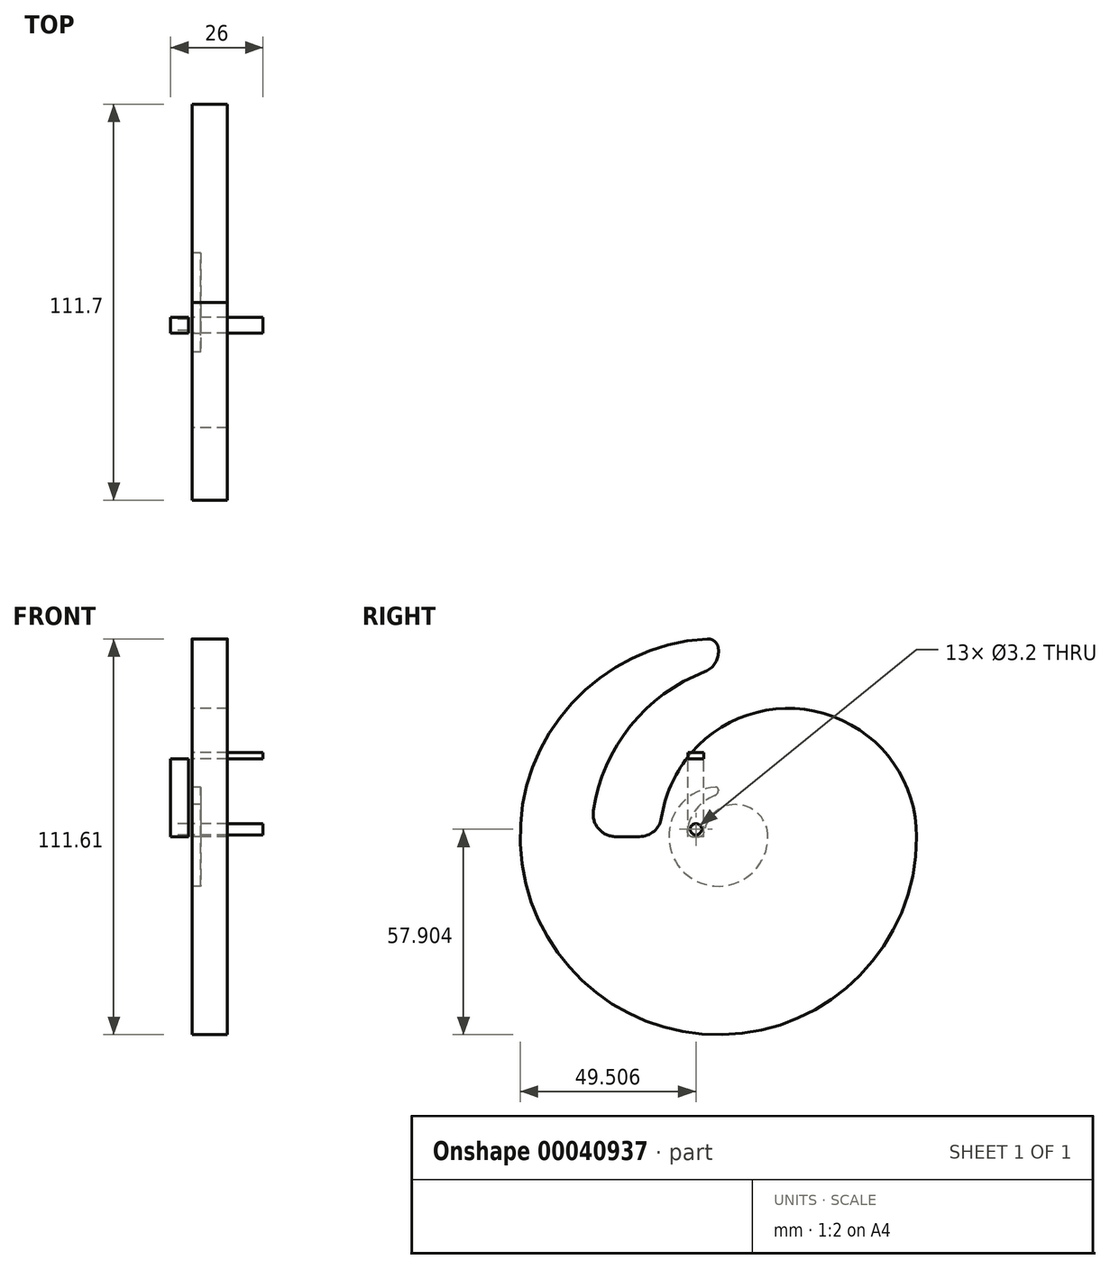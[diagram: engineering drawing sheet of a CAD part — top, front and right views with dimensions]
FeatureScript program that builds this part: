
annotation { "Feature Type Name" : "Feature", "Feature Type Description" : "" }
export const myFeature = defineFeature(function(context is Context, id is Id, definition is map)
    precondition{}
    {
        {
            var Q0;
            Q0=qCreatedBy(makeId("Right.planeOp"),FACE);
            var sketch = newSketch(context, id + "F0", { "sketchPlane" : qUnion([Q0])});
            skArc(sketch, "E0", {"start": v(-3.17, 55.76) * mm, "mid": v(-38.35, -40.6) * mm, "end": v(55.85, 0) * mm});
            skPoint(sketch, "E1", {"position": v(29.62, 47.35) * mm});
            skArc(sketch, "E2", {"start": v(55.85, 0) * mm, "mid": v(22.42, 36.03) * mm, "end": v(-16.02, 5.4) * mm});
            skArc(sketch, "E3", {"start": v(-3.76, 46.53) * mm, "mid": v(-24.8, 31.16) * mm, "end": v(-35.22, 7.28) * mm});
            skLineSegment(sketch, "E4", {"start": v(-28.94, 0) * mm, "end": v(-22.3, 0) * mm});
            skPoint(sketch, "E5.visualSharp", {"position": v(-35.75, 0) * mm});
            skArc(sketch, "E5.filletArc", {"start": v(-35.22, 7.28) * mm, "mid": v(-33.74, 2.2) * mm, "end": v(-28.94, 0) * mm});
            skPoint(sketch, "E6.visualSharp", {"position": v(-16.42, 0) * mm});
            skArc(sketch, "E6.filletArc", {"start": v(-22.3, 0) * mm, "mid": v(-18.15, 1.54) * mm, "end": v(-16.02, 5.4) * mm});
            skLineSegment(sketch, "E7", {"start": v(0, 52.76) * mm, "end": v(0, 52) * mm});
            skPoint(sketch, "E8.visualSharp", {"position": v(0, 47.8) * mm});
            skArc(sketch, "E8.filletArc", {"start": v(-3.76, 46.53) * mm, "mid": v(-1.03, 48.68) * mm, "end": v(0, 52) * mm});
            skPoint(sketch, "E9.visualSharp", {"position": v(0, 55.85) * mm});
            skArc(sketch, "E9.filletArc", {"start": v(0, 52.76) * mm, "mid": v(-0.94, 54.94) * mm, "end": v(-3.17, 55.76) * mm});
            skSolve(sketch);
        }
        {
            var Q0;
            Q0=makeQuery(id+"F0.imprint","IMPRINT",FACE,{"disambiguationData":[TD([[makeQuery(id+"F0.imprint","IMPRINT",EDGE,{"derivedFrom":sQuery(id+"F0.wireOp",EDGE,"E0")}),1.0]])]});
            extrude(context, id + "F1", {"entities" : qUnion([Q0]), "depth" : 10 * mm});
        }
        {
            var Q0;
            Q0=makeQuery(id+"F1.opExtrude","SWEPT_BODY",BODY,{"disambiguationData":[OSD([sQuery(id+"F0.wireOp",EDGE,"E0"),sQuery(id+"F0.wireOp",EDGE,"E2"),sQuery(id+"F0.wireOp",EDGE,"E3"),sQuery(id+"F0.wireOp",EDGE,"E4"),sQuery(id+"F0.wireOp",EDGE,"E5.filletArc"),sQuery(id+"F0.wireOp",EDGE,"E6.filletArc"),sQuery(id+"F0.wireOp",EDGE,"E7"),sQuery(id+"F0.wireOp",EDGE,"E8.filletArc"),sQuery(id+"F0.wireOp",EDGE,"E9.filletArc")])]});
            var Q1;
            Q1=qCreatedBy(makeId("Origin.pointOp"),VERTEX);
            transform(context, id + "F2", {"entities" : qUnion([Q0]), "transformType" : TransformType.SCALE_UNIFORMLY, "scale" : .25, "makeCopy" : true, "scalePoint" : qUnion([Q1])});
        }
        {
            var Q0;
            Q0=qCreatedBy(makeId("Right.planeOp"),FACE);
            var sketch = newSketch(context, id + "F3", { "sketchPlane" : qUnion([Q0])});
            skCircle(sketch, "E10", {"center": v(-6.34, 2.05) * mm, "radius": 1.6 * mm});
            skLineSegment(sketch, "E11.bottom", {"start": v(-4.17, 0) * mm, "end": v(-8.63, 0) * mm});
            skLineSegment(sketch, "E11.top", {"start": v(-4.17, 23.7) * mm, "end": v(-8.63, 23.7) * mm});
            skLineSegment(sketch, "E11.left", {"start": v(-4.17, 0) * mm, "end": v(-4.17, 21.95) * mm});
            skLineSegment(sketch, "E11.right", {"start": v(-8.63, 0) * mm, "end": v(-8.63, 21.95) * mm});
            skLineSegment(sketch, "E12", {"start": v(-8.63, 21.95) * mm, "end": v(-4.17, 21.95) * mm});
            skLineSegment(sketch, "E13", {"start": v(-8.63, 21.95) * mm, "end": v(-8.63, 23.7) * mm});
            skLineSegment(sketch, "E14", {"start": v(-4.17, 21.95) * mm, "end": v(-4.17, 23.7) * mm});
            skSolve(sketch);
        }
        {
            var Q0;
            Q0=makeQuery(id+"F3.imprint","IMPRINT",FACE,{"disambiguationData":[TD([[makeQuery(id+"F3.imprint","IMPRINT",EDGE,{"derivedFrom":sQuery(id+"F3.wireOp",EDGE,"E10")}),1.0]])]});
            var Q1;
            Q1=makeQuery(id+"F3.imprint","IMPRINT",FACE,{"disambiguationData":[TD([[makeQuery(id+"F3.imprint","IMPRINT",EDGE,{"derivedFrom":sQuery(id+"F3.wireOp",EDGE,"E11.top")}),1.0]])]});
            extrude(context, id + "F4", {"entities" : qUnion([Q0, Q1]), "depth" : 20 * mm});
        }
        {
            var Q0;
            Q0=makeQuery(id+"F3.imprint","IMPRINT",FACE,{"disambiguationData":[TD([[makeQuery(id+"F3.imprint","IMPRINT",EDGE,{"derivedFrom":sQuery(id+"F3.wireOp",EDGE,"E10")}),-1.0]])]});
            extrude(context, id + "F5", {"entities" : qUnion([Q0]), "depth" : 5 * mm});
        }
        {
            var Q0;
            Q0=makeQuery(id+"F5.opExtrude","SWEPT_BODY",BODY,{"disambiguationData":[OSD([sQuery(id+"F3.wireOp",EDGE,"E10"),sQuery(id+"F3.wireOp",EDGE,"E11.bottom"),sQuery(id+"F3.wireOp",EDGE,"E11.left"),sQuery(id+"F3.wireOp",EDGE,"E11.right"),sQuery(id+"F3.wireOp",EDGE,"E12")])]});
            transform(context, id + "F6", {"entities" : qUnion([Q0]), "transformType" : TransformType.TRANSLATION_3D, "dx" : -6 * mm, "dy" : 0 * mm, "dz" : 0 * mm, "makeCopy" : false});
        }
    });
